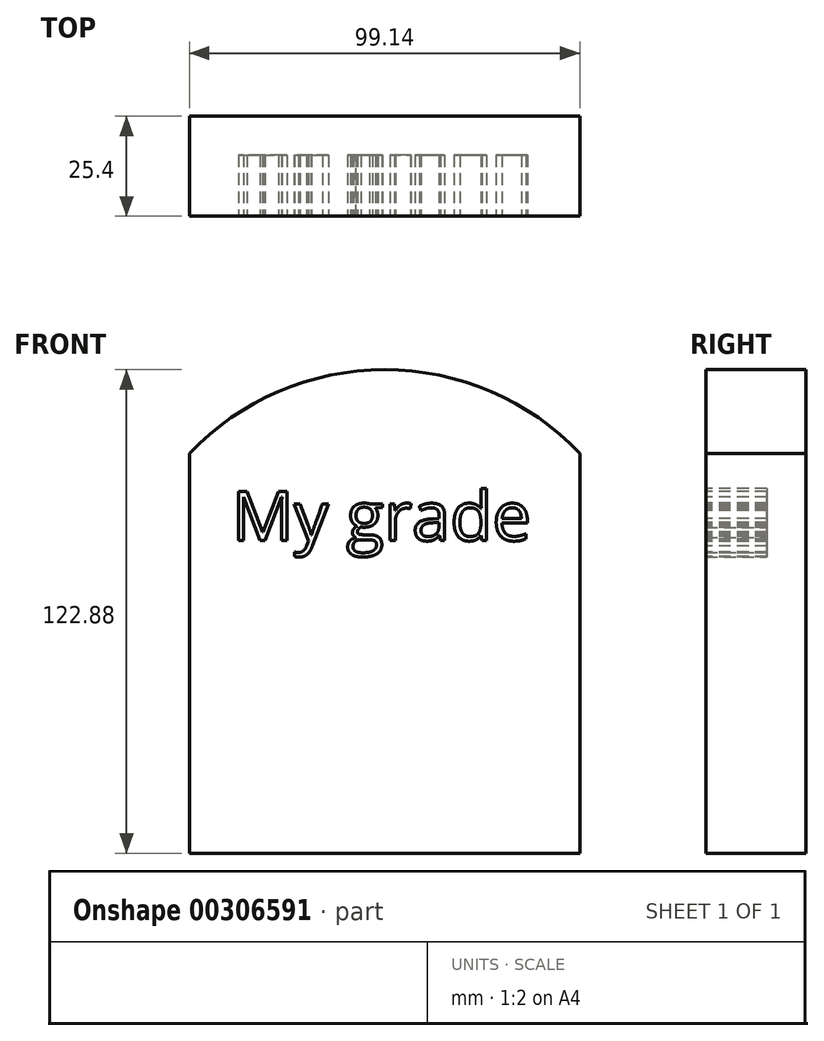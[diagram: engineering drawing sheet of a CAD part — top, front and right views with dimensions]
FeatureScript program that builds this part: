
annotation { "Feature Type Name" : "Feature", "Feature Type Description" : "" }
export const myFeature = defineFeature(function(context is Context, id is Id, definition is map)
    precondition{}
    {
        {
            var Q0;
            Q0=qCreatedBy(makeId("Front.planeOp"),FACE);
            var sketch = newSketch(context, id + "F0", { "sketchPlane" : qUnion([Q0])});
            skLineSegment(sketch, "E0", {"start": v(-44.82, -47.14) * mm, "end": v(54.32, -47.14) * mm});
            skLineSegment(sketch, "E1", {"start": v(-44.82, -47.14) * mm, "end": v(-44.82, 54.46) * mm});
            skLineSegment(sketch, "E2", {"start": v(54.32, -47.14) * mm, "end": v(54.32, 54.46) * mm});
            skArc(sketch, "E3", {"start": v(54.32, 54.46) * mm, "mid": v(4.75, 75.74) * mm, "end": v(-44.82, 54.46) * mm});
            skSolve(sketch);
        }
        {
            var Q0;
            Q0=makeQuery(id+"F0.imprint","IMPRINT",FACE,{"disambiguationData":[TD([[makeQuery(id+"F0.imprint","IMPRINT",EDGE,{"derivedFrom":sQuery(id+"F0.wireOp",EDGE,"E0")}),1.0]])]});
            extrude(context, id + "F1", {"entities" : qUnion([Q0]), "depth" : 25.4 * mm});
        }
        {
            var Q0;
            Q0=makeQuery(id+"F1.opExtrude","CAP_FACE",FACE,{"disambiguationData":[OSD([sQuery(id+"F0.wireOp",EDGE,"E0"),sQuery(id+"F0.wireOp",EDGE,"E1"),sQuery(id+"F0.wireOp",EDGE,"E2"),sQuery(id+"F0.wireOp",EDGE,"E3")])],"isStart":false});
            var sketch = newSketch(context, id + "F2", { "sketchPlane" : qUnion([Q0])});
            skText(sketch, "E4", { "text": "My grade \n", "fontName": "OpenSans-Regular.ttf"});
            const initialGuessF2  = {"E4": [-0.03411, 0.03232, 1, 0, 0.01257]};
            skSetInitialGuess(sketch, initialGuessF2);
            skSolve(sketch);
        }
        {
            var Q0;
            Q0 = qSketchRegion(id + "F2", true);
            extrude(context, id + "F3", {"entities" : qUnion([Q0]), "operationType" : NewBodyOperationType.REMOVE, "oppositeDirection" : true, "depth" : 15.5 * mm});
        }
    });
